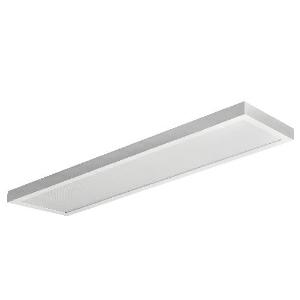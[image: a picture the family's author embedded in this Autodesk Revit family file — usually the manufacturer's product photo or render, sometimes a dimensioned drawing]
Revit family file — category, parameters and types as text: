
# Revit family: ledpanels-sf-p_l12-40w-830_840_542003155900_ef6a
name_source: partatom
category: Lighting Fixtures
units: mm (PartAtom-declared; Revit-internal decimal feet)

## family parameters
Cut with Voids When Loaded = No
Host = Face
Light Source = No
Part Type = Normal
Room Calculation Point = No
Round Connector Dimension = Use Diameter
Shared = No

## types (1)
- LEDPanelS-Sf-P L12-40W-830/840 (1 x LED, 5000 lm, 4000)
    Apparent Load = 40 VA
    Approval mark = CE, ENEC
    CIE Flux Codes = 60 87 97 100 100
    Color Rendering = 80
    Color Temperature = 4000
    Control Gear = Electronic ballast
    Default Elevation = 1800 mm
    Description = Panel Performer Surface Mounted 1274x370mm-40W-5000lm-3/4000K
    Frequency = 60 Hz
    Height = 55 mm
    Lamp = 1 x LED
    Lamp Light Flux = 5000 lm
    Lamp count = 1
    Length = 1274 mm
    Luminous efficacy = 125 lm/W
    Manufacturer = OPPLE
    ModVariant = No
    Model = 542003155900
    Mounting Place = Ceiling
    Mounting Type = Surface mounted
    Number of Poles = 1
    OnlyDefault = Yes
    Power Factor = 1
    Product Name = LEDPanelS-Sf-P L12-40W-830/840
    Product group = Ceiling mounted luminaire
    ProductGroupID = 3
    Protection Class = Protection class II
    Protection Degree = IP 20
    RLX_Detail_Level = 1
    RLX_Emergency_Light_Flux = 0 lm
    RLX_Emergency_Type = 0
    RLX_Emergency_Type_DB = No
    RlxData = <blob elided: 95509 chars, md5=34fed8ac>
    Socket = socket
    Standby Power = 0 W
    System Light Flux = 5000 lm
    System Power = 40 W
    Type Comments = Product without accessories
    Type Image = web_surface_pl.jpg
    URL = http://relux.com
    VarID = ---
    Voltage = 230 V
    Voltage Range = 220-240 V
    Weight = 0.00 kg
    Width = 370 mm

## geometry (parser evidence)
native form markers: Blend x4, Sweep x11
no freeform markers — native parametric forms only
